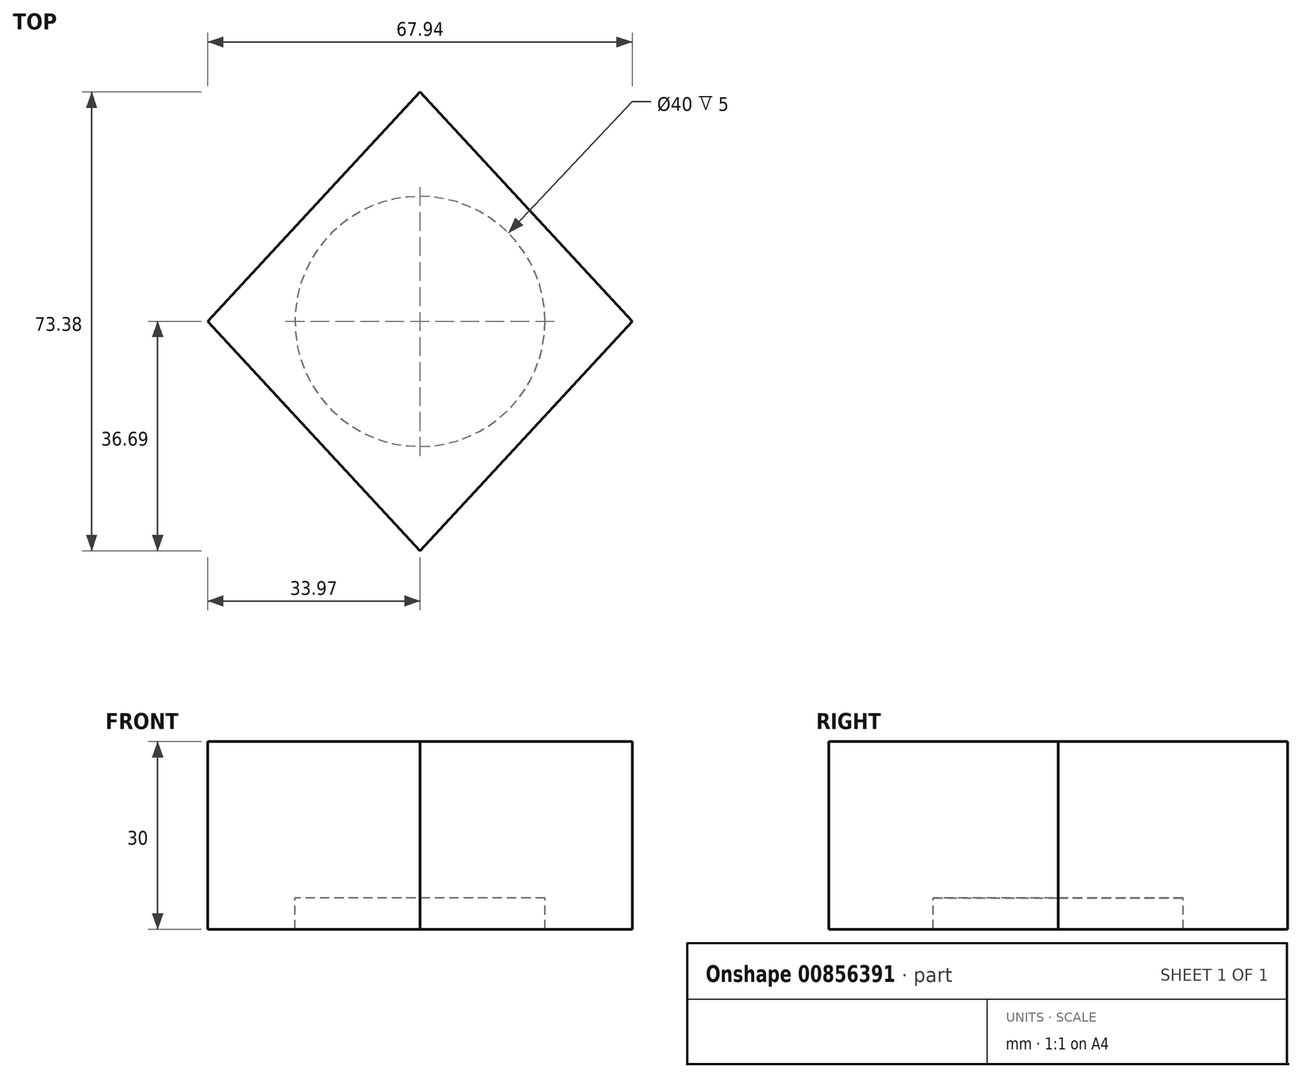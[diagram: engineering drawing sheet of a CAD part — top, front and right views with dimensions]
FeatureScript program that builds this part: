
annotation { "Feature Type Name" : "Feature", "Feature Type Description" : "" }
export const myFeature = defineFeature(function(context is Context, id is Id, definition is map)
    precondition{}
    {
        {
            var Q0;
            Q0=qCreatedBy(makeId("Top.planeOp"),FACE);
            var sketch = newSketch(context, id + "F0", { "sketchPlane" : qUnion([Q0])});
            skLineSegment(sketch, "E0", {"start": v(0, 36.7) * mm, "end": v(-33.97, 0) * mm});
            skLineSegment(sketch, "E1", {"start": v(-33.97, 0) * mm, "end": v(0, -36.7) * mm});
            skLineSegment(sketch, "E2", {"start": v(0, -36.7) * mm, "end": v(33.97, 0) * mm});
            skLineSegment(sketch, "E3", {"start": v(33.97, 0) * mm, "end": v(0, 36.7) * mm});
            skCircle(sketch, "E4", {"center": v(0, 0) * mm, "radius": 20 * mm});
            skSolve(sketch);
        }
        {
            var Q0;
            Q0 = qSketchRegion(id + "F0", true);
            extrude(context, id + "F1", {"entities" : qUnion([Q0]), "depth" : 25 * mm, "offsetDistance" : 25 * mm});
        }
        {
            var Q0;
            Q0=makeQuery(id+"F0.imprint","IMPRINT",FACE,{"disambiguationData":[TD([[makeQuery(id+"F0.imprint","IMPRINT",EDGE,{"derivedFrom":sQuery(id+"F0.wireOp",EDGE,"E0")}),1.0]])]});
            extrude(context, id + "F2", {"entities" : qUnion([Q0]), "operationType" : NewBodyOperationType.ADD, "depth" : 10 * mm, "offsetDistance" : 25 * mm});
        }
        {
            var Q0;
            Q0=makeQuery(id+"F0.imprint","IMPRINT",FACE,{"disambiguationData":[TD([[makeQuery(id+"F0.imprint","IMPRINT",EDGE,{"derivedFrom":sQuery(id+"F0.wireOp",EDGE,"E0")}),1.0]])]});
            var Q1;
            Q1=makeQuery(id+"F0.imprint","IMPRINT",FACE,{"disambiguationData":[TD([[makeQuery(id+"F0.imprint","IMPRINT",EDGE,{"derivedFrom":sQuery(id+"F0.wireOp",EDGE,"E4")}),1.0]])]});
            extrude(context, id + "F3", {"entities" : qUnion([Q0, Q1]), "operationType" : NewBodyOperationType.ADD, "depth" : 15 * mm, "offsetDistance" : 25 * mm});
        }
        {
            var Q0;
            Q0=makeQuery(id+"F0.imprint","IMPRINT",FACE,{"disambiguationData":[TD([[makeQuery(id+"F0.imprint","IMPRINT",EDGE,{"derivedFrom":sQuery(id+"F0.wireOp",EDGE,"E4")}),1.0]])]});
            extrude(context, id + "F4", {"entities" : qUnion([Q0]), "operationType" : NewBodyOperationType.ADD, "depth" : 25 * mm, "offsetDistance" : 25 * mm});
        }
        {
            var Q0;
            Q0=makeQuery(id+"F0.imprint","IMPRINT",FACE,{"disambiguationData":[TD([[makeQuery(id+"F0.imprint","IMPRINT",EDGE,{"derivedFrom":sQuery(id+"F0.wireOp",EDGE,"E0")}),1.0]])]});
            extrude(context, id + "F5", {"entities" : qUnion([Q0]), "operationType" : NewBodyOperationType.ADD, "oppositeDirection" : true, "depth" : 5 * mm, "offsetDistance" : 25 * mm});
        }
        {
            var Q0;
            Q0=makeQuery(id+"F0.imprint","IMPRINT",FACE,{"disambiguationData":[TD([[makeQuery(id+"F0.imprint","IMPRINT",EDGE,{"derivedFrom":sQuery(id+"F0.wireOp",EDGE,"E4")}),1.0]])]});
            extrude(context, id + "F6", {"entities" : qUnion([Q0]), "operationType" : NewBodyOperationType.ADD, "depth" : 10 * mm, "offsetDistance" : 25 * mm});
        }
        {
            var Q0;
            Q0=makeQuery(id+"F0.imprint","IMPRINT",FACE,{"disambiguationData":[TD([[makeQuery(id+"F0.imprint","IMPRINT",EDGE,{"derivedFrom":sQuery(id+"F0.wireOp",EDGE,"E4")}),1.0]])]});
            extrude(context, id + "F7", {"entities" : qUnion([Q0]), "operationType" : NewBodyOperationType.ADD, "depth" : 10 * mm, "offsetDistance" : 25 * mm});
        }
        {
            var Q0;
            Q0=makeQuery(id+"F0.imprint","IMPRINT",FACE,{"disambiguationData":[TD([[makeQuery(id+"F0.imprint","IMPRINT",EDGE,{"derivedFrom":sQuery(id+"F0.wireOp",EDGE,"E4")}),1.0]])]});
            var Q1;
            Q1=makeQuery(id+"F5.opExtrude","CAP_FACE",FACE,{"disambiguationData":[OSD([sQuery(id+"F0.wireOp",EDGE,"E0"),sQuery(id+"F0.wireOp",EDGE,"E1"),sQuery(id+"F0.wireOp",EDGE,"E2"),sQuery(id+"F0.wireOp",EDGE,"E3"),sQuery(id+"F0.wireOp",EDGE,"E4")])],"isStart":false});
            extrude(context, id + "F8", {"entities" : qUnion([Q0, Q1]), "operationType" : NewBodyOperationType.ADD, "depth" : 10 * mm, "offsetDistance" : 25 * mm});
        }
    });
